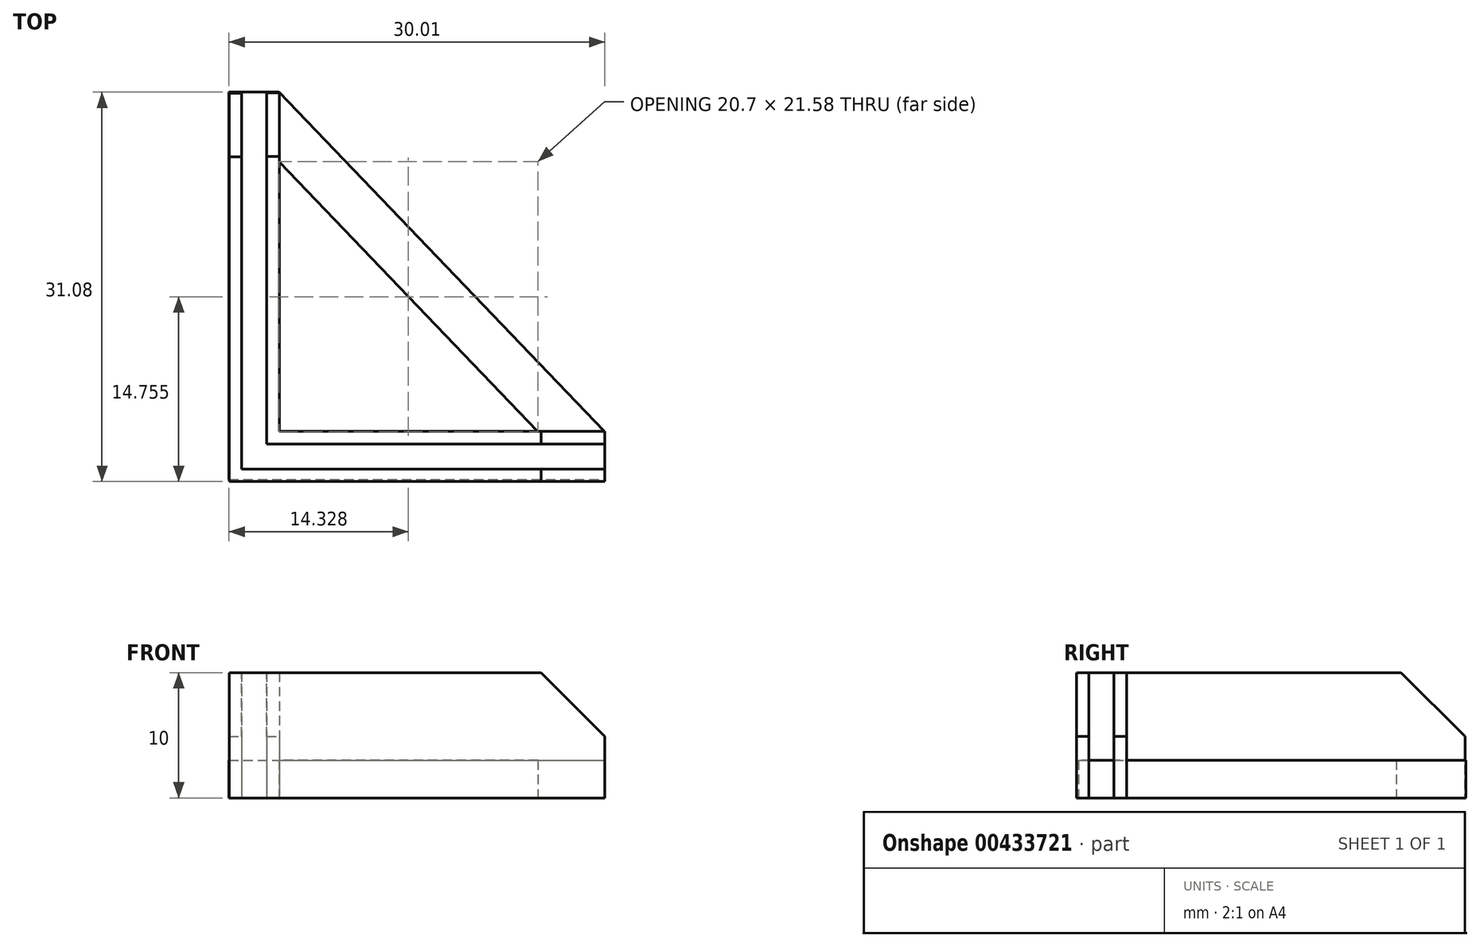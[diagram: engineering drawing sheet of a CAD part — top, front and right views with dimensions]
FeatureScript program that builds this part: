
annotation { "Feature Type Name" : "Feature", "Feature Type Description" : "" }
export const myFeature = defineFeature(function(context is Context, id is Id, definition is map)
    precondition{}
    {
        {
            var Q0;
            Q0=qCreatedBy(makeId("Top.planeOp"),FACE);
            var sketch = newSketch(context, id + "F0", { "sketchPlane" : qUnion([Q0])});
            skLineSegment(sketch, "E0.bottom", {"start": v(-30.95, 25.43) * mm, "end": v(-31.95, 25.43) * mm});
            skLineSegment(sketch, "E0.left", {"start": v(-30.95, 25.43) * mm, "end": v(-30.95, -4.57) * mm});
            skLineSegment(sketch, "E0.right", {"start": v(-31.95, 25.43) * mm, "end": v(-31.95, -4.57) * mm});
            skLineSegment(sketch, "E1.bottom", {"start": v(-30.95, -4.57) * mm, "end": v(-1.95, -4.57) * mm});
            skLineSegment(sketch, "E1.top", {"start": v(-31.95, -5.57) * mm, "end": v(-1.95, -5.57) * mm});
            skLineSegment(sketch, "E1.left", {"start": v(-31.95, -4.57) * mm, "end": v(-31.95, -5.57) * mm});
            skLineSegment(sketch, "E1.right", {"start": v(-1.95, -4.57) * mm, "end": v(-1.95, -5.57) * mm});
            skLineSegment(sketch, "E2.bottom", {"start": v(-28.95, 25.45) * mm, "end": v(-27.95, 25.45) * mm});
            skLineSegment(sketch, "E2.top", {"start": v(-28.95, -2.57) * mm, "end": v(-27.95, -2.57) * mm});
            skLineSegment(sketch, "E2.left", {"start": v(-28.95, 25.45) * mm, "end": v(-28.95, -2.57) * mm});
            skLineSegment(sketch, "E2.right", {"start": v(-27.95, 25.45) * mm, "end": v(-27.95, -1.57) * mm});
            skLineSegment(sketch, "E3.bottom", {"start": v(-1.95, -2.57) * mm, "end": v(-27.95, -2.57) * mm});
            skLineSegment(sketch, "E3.top", {"start": v(-1.95, -1.57) * mm, "end": v(-27.95, -1.57) * mm});
            skLineSegment(sketch, "E3.left", {"start": v(-1.95, -2.57) * mm, "end": v(-1.95, -1.57) * mm});
            skPoint(sketch, "E4.end.orphan", {"position": v(-24.35, -2.57) * mm});
            skPoint(sketch, "E5.end.orphan", {"position": v(-5, -2.57) * mm});
            skPoint(sketch, "E6.end.orphan", {"position": v(-28.95, 19.89) * mm});
            skSolve(sketch);
        }
        {
            var Q0;
            Q0 = qSketchRegion(id + "F0", true);
            extrude(context, id + "F1", {"entities" : qUnion([Q0]), "depth" : 10 * mm, "offsetDistance" : 25.4 * mm});
        }
        {
            var Q0;
            Q0=qCreatedBy(makeId("Top.planeOp"),FACE);
            var sketch = newSketch(context, id + "F2", { "sketchPlane" : qUnion([Q0])});
            skLineSegment(sketch, "E7.bottom", {"start": v(-31.96, 25.51) * mm, "end": v(-27.98, 25.51) * mm});
            skLineSegment(sketch, "E7.top", {"start": v(-31.96, -5.39) * mm, "end": v(-27.98, -5.39) * mm});
            skLineSegment(sketch, "E7.left", {"start": v(-31.96, 25.51) * mm, "end": v(-31.96, -5.39) * mm});
            skLineSegment(sketch, "E7.right", {"start": v(-27.98, 25.51) * mm, "end": v(-27.98, -5.39) * mm});
            skLineSegment(sketch, "E8.bottom", {"start": v(-1.97, -5.39) * mm, "end": v(-27.98, -5.39) * mm});
            skLineSegment(sketch, "E8.top", {"start": v(-1.97, -1.6) * mm, "end": v(-27.98, -1.6) * mm});
            skLineSegment(sketch, "E8.left", {"start": v(-1.97, -5.39) * mm, "end": v(-1.97, -1.6) * mm});
            skLineSegment(sketch, "E8.right", {"start": v(-27.98, -5.39) * mm, "end": v(-27.98, -1.6) * mm});
            skLineSegment(sketch, "E9", {"start": v(-27.98, 25.51) * mm, "end": v(-1.97, -1.6) * mm});
            skLineSegment(sketch, "E10", {"start": v(-7.28, -1.6) * mm, "end": v(-27.98, 19.97) * mm});
            skSolve(sketch);
        }
        {
            var Q0;
            {var subQ3=sQuery(id+"F2.wireOp",EDGE,"E9");var subQ8=sQuery(id+"F2.wireOp",EDGE,"E8.bottom");var subQ11=sQuery(id+"F2.wireOp",EDGE,"E7.bottom");Q0=qUnion([makeQuery(id+"F2.imprint","IMPRINT",FACE,{"disambiguationData":[TD([[makeQuery(id+"F2.imprint","IMPRINT",EDGE,{"derivedFrom":subQ11}),-1.0]])]}),makeQuery(id+"F2.imprint","IMPRINT",FACE,{"disambiguationData":[TD([[makeQuery(id+"F2.imprint","IMPRINT",EDGE,{"derivedFrom":subQ3}),-1.0]])]}),makeQuery(id+"F2.imprint","IMPRINT",FACE,{"disambiguationData":[TD([[makeQuery(id+"F2.imprint","IMPRINT",EDGE,{"derivedFrom":subQ8}),-1.0]])]})]);}
            extrude(context, id + "F3", {"entities" : qUnion([Q0]), "depth" : 3 * mm, "offsetDistance" : 25.4 * mm});
        }
        {
            var Q0;
            Q0=makeQuery(id+"F1.opExtrude","CAP_EDGE",EDGE,{"disambiguationData":[OSD([sQuery(id+"F0.wireOp",EDGE,"E0.bottom")])],"isStart":false});
            chamfer(context, id + "F4", {"entities" : qUnion([Q0]), "width" : 5.08 * mm, "tangentPropagation" : true});
        }
        {
            var Q0;
            Q0=makeQuery(id+"F1.opExtrude","CAP_EDGE",EDGE,{"disambiguationData":[OSD([sQuery(id+"F0.wireOp",EDGE,"E2.bottom")])],"isStart":false});
            chamfer(context, id + "F5", {"entities" : qUnion([Q0]), "width" : 5.08 * mm, "tangentPropagation" : true});
        }
        {
            var Q0;
            Q0=makeQuery(id+"F1.opExtrude","CAP_EDGE",EDGE,{"disambiguationData":[OSD([sQuery(id+"F0.wireOp",EDGE,"E3.left")])],"isStart":false});
            var Q1;
            Q1=makeQuery(id+"F1.opExtrude","CAP_EDGE",EDGE,{"disambiguationData":[OSD([sQuery(id+"F0.wireOp",EDGE,"E1.right")])],"isStart":false});
            chamfer(context, id + "F6", {"entities" : qUnion([Q0, Q1]), "width" : 5.08 * mm, "tangentPropagation" : true});
        }
    });
